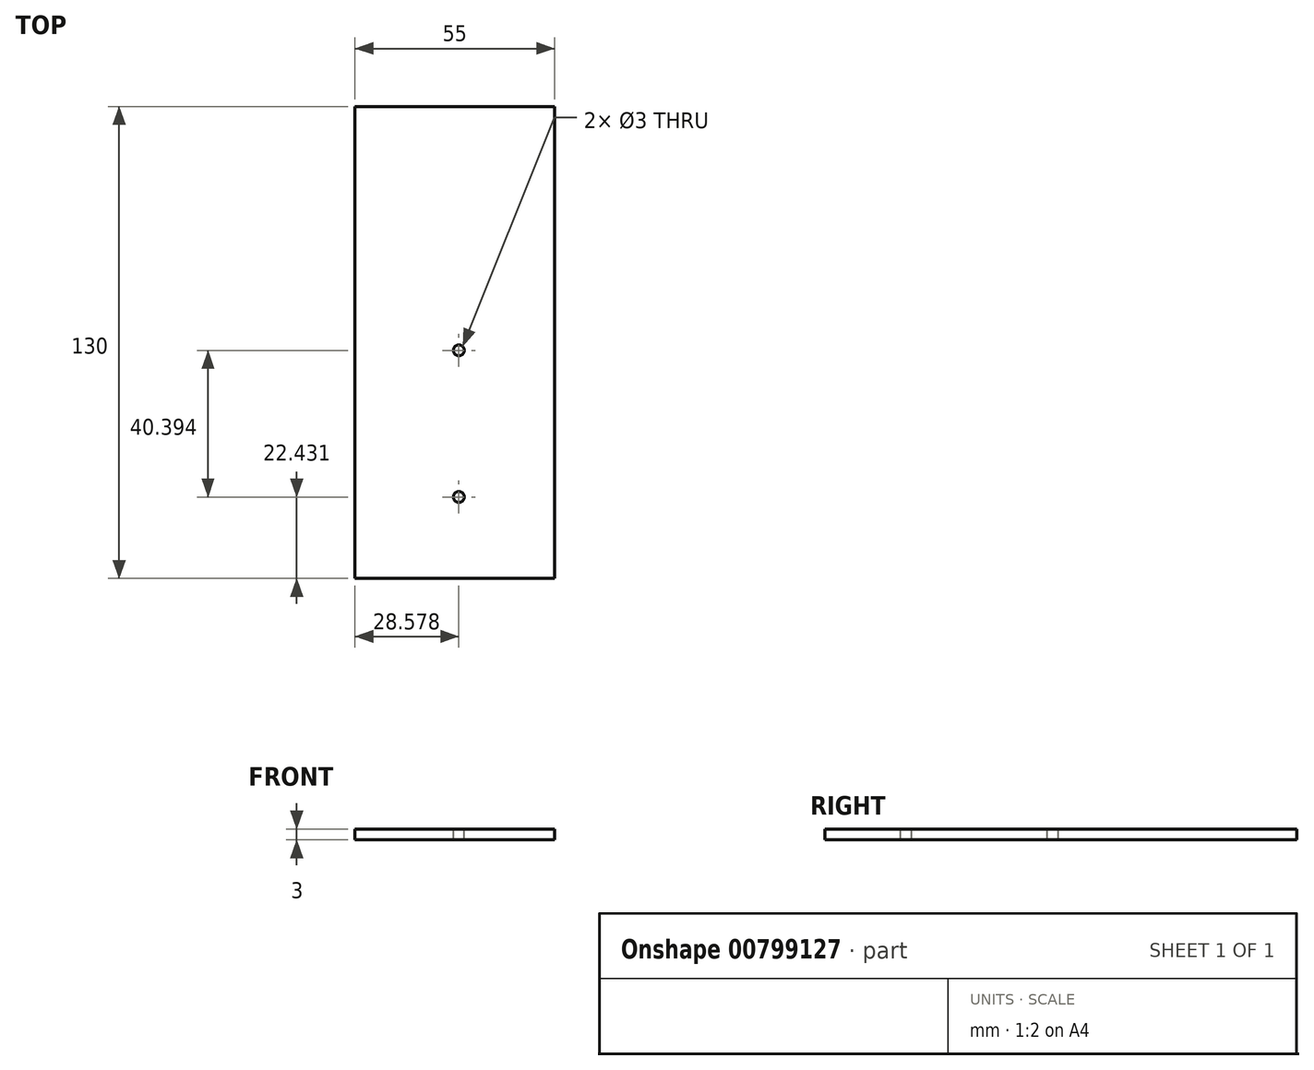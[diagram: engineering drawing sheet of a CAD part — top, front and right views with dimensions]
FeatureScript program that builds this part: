
annotation { "Feature Type Name" : "Feature", "Feature Type Description" : "" }
export const myFeature = defineFeature(function(context is Context, id is Id, definition is map)
    precondition{}
    {
        {
            var Q0;
            Q0=qCreatedBy(makeId("Top.planeOp"),FACE);
            var sketch = newSketch(context, id + "F0", { "sketchPlane" : qUnion([Q0])});
            skLineSegment(sketch, "E0.bottom", {"start": v(0, 0) * mm, "end": v(55, 0) * mm});
            skLineSegment(sketch, "E0.top", {"start": v(0, 130) * mm, "end": v(55, 130) * mm});
            skLineSegment(sketch, "E0.left", {"start": v(0, 0) * mm, "end": v(0, 130) * mm});
            skLineSegment(sketch, "E0.right", {"start": v(55, 0) * mm, "end": v(55, 130) * mm});
            skSolve(sketch);
        }
        {
            var Q0;
            Q0=makeQuery(id+"F0.imprint","IMPRINT",FACE,{"disambiguationData":[TD([[makeQuery(id+"F0.imprint","IMPRINT",EDGE,{"derivedFrom":sQuery(id+"F0.wireOp",EDGE,"E0.bottom")}),1.0]])]});
            extrude(context, id + "F1", {"entities" : qUnion([Q0]), "depth" : 3 * mm, "offsetDistance" : 25 * mm});
        }
        {
            var Q0;
            Q0=makeQuery(id+"F1.opExtrude","CAP_FACE",FACE,{"disambiguationData":[OSD([sQuery(id+"F0.wireOp",EDGE,"E0.bottom"),sQuery(id+"F0.wireOp",EDGE,"E0.top"),sQuery(id+"F0.wireOp",EDGE,"E0.left"),sQuery(id+"F0.wireOp",EDGE,"E0.right")])],"isStart":false});
            var sketch = newSketch(context, id + "F2", { "sketchPlane" : qUnion([Q0])});
            skSolve(sketch);
        }
        {
            var Q0;
            Q0=makeQuery(id+"F2.imprint","IMPRINT",FACE,{"disambiguationData":[TD([[makeQuery(id+"F2.imprint","IMPRINT",EDGE,{"derivedFrom":makeQuery(id+"F1.opExtrude","CAP_EDGE",EDGE,{"disambiguationData":[OSD([sQuery(id+"F0.wireOp",EDGE,"E0.bottom")])],"isStart":false})}),1.0]])]});
            var sketch = newSketch(context, id + "F3", { "sketchPlane" : qUnion([Q0])});
            skLineSegment(sketch, "E1", {"start": v(28.58, 22.43) * mm, "end": v(28.58, 62.83) * mm});
            skSolve(sketch);
        }
        {
            var Q0;
            Q0=sQuery(id+"F3.wireOp",VERTEX,"E1.start");
            var Q1;
            Q1=sQuery(id+"F3.wireOp",VERTEX,"E1.end");
            var Q2;
            Q2=makeQuery(id+"F1.opExtrude","SWEPT_BODY",BODY,{"disambiguationData":[OSD([sQuery(id+"F0.wireOp",EDGE,"E0.bottom"),sQuery(id+"F0.wireOp",EDGE,"E0.top"),sQuery(id+"F0.wireOp",EDGE,"E0.left"),sQuery(id+"F0.wireOp",EDGE,"E0.right")])]});
            hole(context, id + "F4", {"style" : HoleStyle.SIMPLE, "endStyle" : HoleEndStyle.THROUGH, "holeDiameter" : 3 * mm, "majorDiameter" : 5 * mm, "isTappedThrough" : true, "tappedDepth" : 12 * mm, "tapClearance" : 3, "locations" : qUnion([Q0, Q1]), "scope" : qUnion([Q2])});
        }
    });
